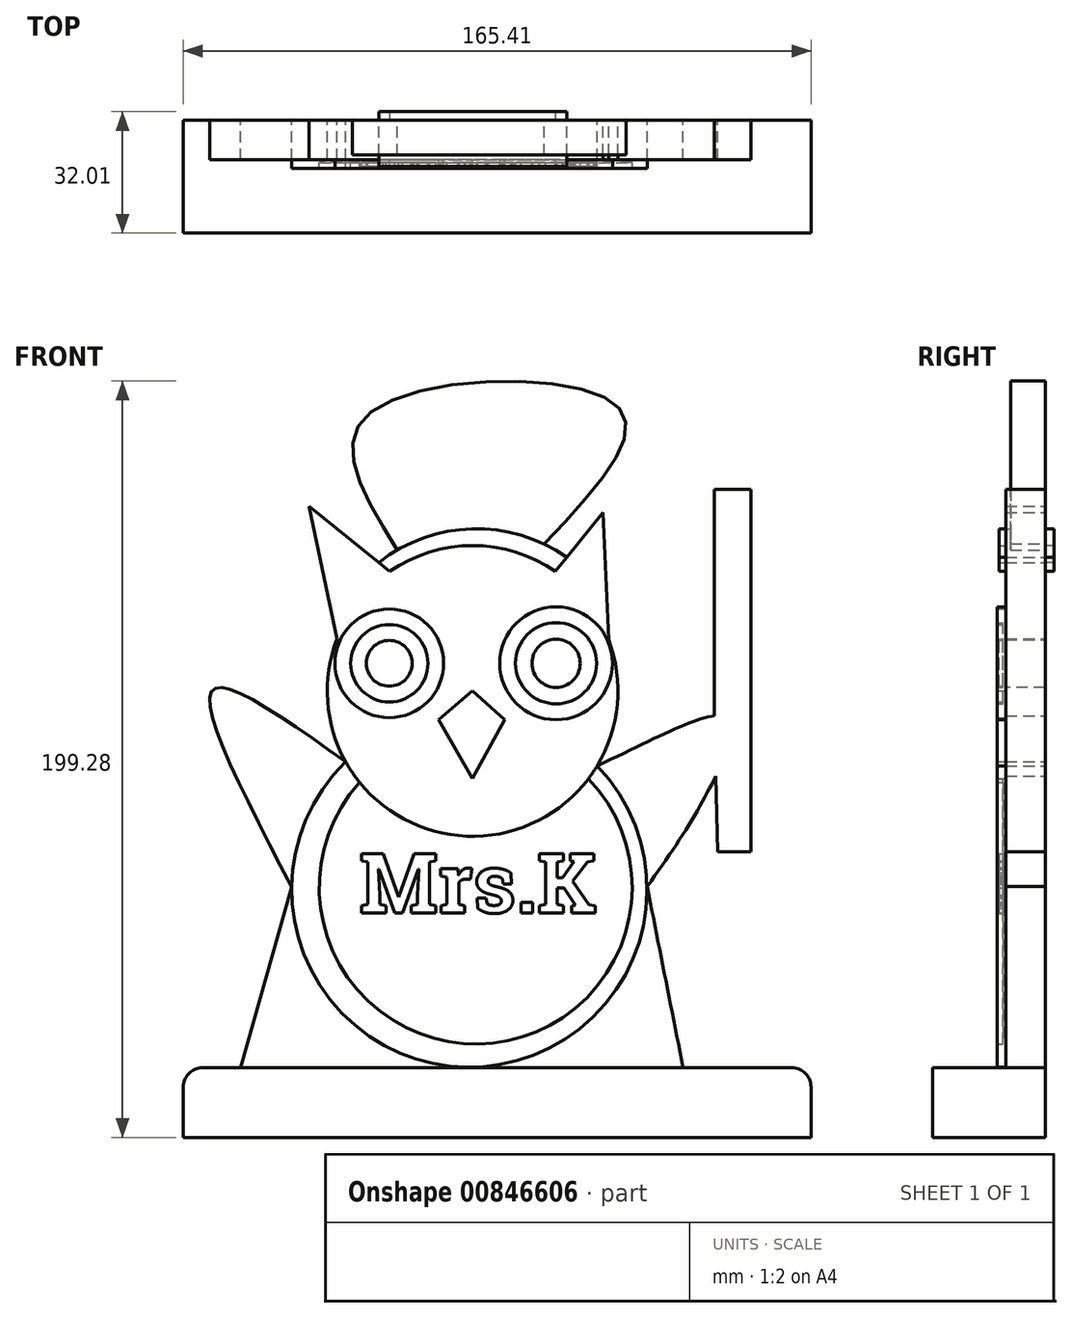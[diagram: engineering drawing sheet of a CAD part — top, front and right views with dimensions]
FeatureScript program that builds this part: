
annotation { "Feature Type Name" : "Feature", "Feature Type Description" : "" }
export const myFeature = defineFeature(function(context is Context, id is Id, definition is map)
    precondition{}
    {
        {
            var Q0;
            Q0=qCreatedBy(makeId("Front.planeOp"),FACE);
            var sketch = newSketch(context, id + "F0", { "sketchPlane" : qUnion([Q0])});
            skLineSegment(sketch, "E0.bottom", {"start": v(-76.22, -47.61) * mm, "end": v(89.19, -47.61) * mm});
            skLineSegment(sketch, "E0.top", {"start": v(-76.22, -65.94) * mm, "end": v(89.19, -65.94) * mm});
            skLineSegment(sketch, "E0.left", {"start": v(-76.22, -47.61) * mm, "end": v(-76.22, -65.94) * mm});
            skLineSegment(sketch, "E0.right", {"start": v(89.19, -47.61) * mm, "end": v(89.19, -65.94) * mm});
            skCircle(sketch, "E1", {"center": v(0, 51.72) * mm, "radius": 38.3 * mm});
            skArc(sketch, "E2", {"start": v(-33.43, 33) * mm, "mid": v(-1.58, -47.43) * mm, "end": v(32.82, 31.96) * mm});
            skArc(sketch, "E3", {"start": v(-29.76, 27.6) * mm, "mid": v(1.5, -41.3) * mm, "end": v(30.51, 28.56) * mm});
            skFitSpline(sketch, "E4", {"points": [v(-47.65, 0) * mm, v(-61.14, -47.61) * mm], "startDerivative": vector(-13.49, -47.61) * mm, "endDerivative": vector(-13.49, -47.61) * mm});
            skFitSpline(sketch, "E5", {"points": [v(45.99, 0.18) * mm, v(55.5, -47.61) * mm], "startDerivative": vector(9.56, -47.79) * mm, "endDerivative": vector(9.56, -47.79) * mm});
            skFitSpline(sketch, "E6", {"points": [v(-47.65, 0) * mm, v(-68.41, 52.03) * mm, v(-33.43, 33) * mm], "startDerivative": vector(-69.4, 133.2) * mm, "endDerivative": vector(102.73, -73.03) * mm});
            skFitSpline(sketch, "E7", {"points": [v(45.99, 0.18) * mm, v(67, 44.16) * mm, v(32.82, 31.96) * mm], "startDerivative": vector(84.02, 113.87) * mm, "endDerivative": vector(-114.08, -53.46) * mm});
            skLineSegment(sketch, "E8", {"start": v(-35.76, 65.45) * mm, "end": v(-43.12, 100.4) * mm});
            skLineSegment(sketch, "E9", {"start": v(-43.12, 100.4) * mm, "end": v(-21.83, 83.2) * mm});
            skLineSegment(sketch, "E10", {"start": v(21.83, 83.2) * mm, "end": v(34.4, 98.75) * mm});
            skLineSegment(sketch, "E11", {"start": v(34.4, 98.75) * mm, "end": v(35.85, 65.2) * mm});
            skCircle(sketch, "E12", {"center": v(-21.94, 58.99) * mm, "radius": 14.31 * mm});
            skCircle(sketch, "E13", {"center": v(-21.94, 58.99) * mm, "radius": 10.2 * mm});
            skCircle(sketch, "E14", {"center": v(-21.94, 58.99) * mm, "radius": 6.04 * mm});
            skCircle(sketch, "E15", {"center": v(22, 58.99) * mm, "radius": 14.86 * mm});
            skCircle(sketch, "E16", {"center": v(22, 58.99) * mm, "radius": 10.7 * mm});
            skCircle(sketch, "E17", {"center": v(22, 58.99) * mm, "radius": 6.35 * mm});
            skLineSegment(sketch, "E18", {"start": v(0, 51.72) * mm, "end": v(-8.98, 44.13) * mm});
            skLineSegment(sketch, "E19", {"start": v(-8.98, 44.13) * mm, "end": v(0, 28.64) * mm});
            skLineSegment(sketch, "E20", {"start": v(0, 28.64) * mm, "end": v(8.4, 44.13) * mm});
            skLineSegment(sketch, "E21", {"start": v(8.4, 44.13) * mm, "end": v(0, 51.72) * mm});
            skText(sketch, "E22", { "text": "Mrs.K", "fontName": "RobotoSlab-Bold.ttf"});
            skLineSegment(sketch, "E23", {"start": v(63.66, 44.16) * mm, "end": v(63.66, 104.79) * mm});
            skLineSegment(sketch, "E24", {"start": v(63.66, 104.79) * mm, "end": v(73.38, 104.79) * mm});
            skLineSegment(sketch, "E25", {"start": v(73.38, 104.79) * mm, "end": v(73.38, 9.38) * mm});
            skLineSegment(sketch, "E26", {"start": v(73.38, 9.38) * mm, "end": v(64.59, 9.38) * mm});
            skLineSegment(sketch, "E27", {"start": v(64.59, 9.38) * mm, "end": v(63.66, 44.16) * mm});
            skArc(sketch, "E28", {"start": v(24.85, 86.92) * mm, "mid": v(-0.18, 94.42) * mm, "end": v(-24.74, 85.55) * mm});
            skFitSpline(sketch, "E29", {"points": [v(-19.82, 88.87) * mm, v(-27.76, 124.4) * mm, v(38.2, 126.66) * mm, v(18.85, 90.41) * mm], "startDerivative": vector(-86.87, 139.97) * mm, "endDerivative": vector(-130.42, -137.65) * mm});
            const initialGuessF0  = {"E22": [-0.02985, -0.00677, 1, 0, 0.0158]};
            skSetInitialGuess(sketch, initialGuessF0);
            skSolve(sketch);
        }
        {
            var Q0;
            Q0=makeQuery(id+"F0.imprint","IMPRINT",FACE,{"disambiguationData":[TD([[makeQuery(id+"F0.imprint","IMPRINT",EDGE,{"derivedFrom":sQuery(id+"F0.wireOp",EDGE,"E0.top")}),1.0]])]});
            extrude(context, id + "F1", {"entities" : qUnion([Q0]), "depth" : 29.72 * mm, "offsetDistance" : 25.4 * mm});
        }
        {
            var Q0;
            {var subQ0=sQuery(id+"F0.wireOp",EDGE,"E6");Q0=makeQuery(id+"F0.imprint","IMPRINT",FACE,{"disambiguationData":[TD([[makeQuery(id+"F0.imprint","IMPRINT",EDGE,{"derivedFrom":subQ0}),-1.0]])]});}
            var Q1;
            {var subQ0=sQuery(id+"F0.wireOp",EDGE,"E8");Q1=makeQuery(id+"F0.imprint","IMPRINT",FACE,{"disambiguationData":[TD([[makeQuery(id+"F0.imprint","IMPRINT",EDGE,{"derivedFrom":subQ0}),-1.0]])]});}
            var Q2;
            {var subQ0=sQuery(id+"F0.wireOp",EDGE,"E10");Q2=makeQuery(id+"F0.imprint","IMPRINT",FACE,{"disambiguationData":[TD([[makeQuery(id+"F0.imprint","IMPRINT",EDGE,{"derivedFrom":subQ0}),-1.0]])]});}
            var Q3;
            Q3=makeQuery(id+"F0.imprint","IMPRINT",FACE,{"disambiguationData":[TD([[makeQuery(id+"F0.imprint","IMPRINT",EDGE,{"derivedFrom":sQuery(id+"F0.wireOp",EDGE,"E12")}),-1.0]])]});
            var Q4;
            {var subQ0=sQuery(id+"F0.wireOp",EDGE,"E7");Q4=makeQuery(id+"F0.imprint","IMPRINT",FACE,{"disambiguationData":[TD([[makeQuery(id+"F0.imprint","IMPRINT",EDGE,{"derivedFrom":subQ0}),1.0]])]});}
            var Q5;
            {var subQ0=sQuery(id+"F0.wireOp",EDGE,"E4");Q5=makeQuery(id+"F0.imprint","IMPRINT",FACE,{"disambiguationData":[TD([[makeQuery(id+"F0.imprint","IMPRINT",EDGE,{"derivedFrom":subQ0}),1.0]])]});}
            extrude(context, id + "F2", {"entities" : qUnion([Q0, Q1, Q2, Q3, Q4, Q5]), "operationType" : NewBodyOperationType.ADD, "depth" : 10.4 * mm, "offsetDistance" : 25.4 * mm});
        }
        {
            var Q0;
            Q0=makeQuery(id+"F0.imprint","IMPRINT",FACE,{"disambiguationData":[TD([[makeQuery(id+"F0.imprint","IMPRINT",EDGE,{"derivedFrom":sQuery(id+"F0.wireOp",EDGE,"E12")}),1.0]])]});
            var Q1;
            Q1=makeQuery(id+"F0.imprint","IMPRINT",FACE,{"disambiguationData":[TD([[makeQuery(id+"F0.imprint","IMPRINT",EDGE,{"derivedFrom":sQuery(id+"F0.wireOp",EDGE,"E15")}),1.0]])]});
            var Q2;
            Q2=makeQuery(id+"F0.imprint","IMPRINT",FACE,{"disambiguationData":[TD([[makeQuery(id+"F0.imprint","IMPRINT",EDGE,{"derivedFrom":sQuery(id+"F0.wireOp",EDGE,"E18")}),1.0]])]});
            var Q3;
            {var subQ7=sQuery(id+"F0.wireOp",EDGE,"E3");Q3=makeQuery(id+"F0.imprint","IMPRINT",FACE,{"disambiguationData":[TD([[makeQuery(id+"F0.imprint","IMPRINT",EDGE,{"derivedFrom":subQ7}),-1.0]])]});}
            extrude(context, id + "F3", {"entities" : qUnion([Q0, Q1, Q2, Q3]), "operationType" : NewBodyOperationType.ADD, "depth" : 12.7 * mm, "offsetDistance" : 25.4 * mm});
        }
        {
            var Q0;
            Q0=makeQuery(id+"F0.imprint","IMPRINT",FACE,{"disambiguationData":[TD([[makeQuery(id+"F0.imprint","IMPRINT",EDGE,{"derivedFrom":sQuery(id+"F0.wireOp",EDGE,"E16")}),1.0]])]});
            var Q1;
            Q1=makeQuery(id+"F0.imprint","IMPRINT",FACE,{"disambiguationData":[TD([[makeQuery(id+"F0.imprint","IMPRINT",EDGE,{"derivedFrom":sQuery(id+"F0.wireOp",EDGE,"E13")}),1.0]])]});
            var Q2;
            {var subQ0=sQuery(id+"F0.wireOp",EDGE,"E3");Q2=makeQuery(id+"F0.imprint","IMPRINT",FACE,{"disambiguationData":[TD([[makeQuery(id+"F0.imprint","IMPRINT",EDGE,{"derivedFrom":subQ0}),1.0]])]});}
            extrude(context, id + "F4", {"entities" : qUnion([Q0, Q1, Q2]), "operationType" : NewBodyOperationType.ADD, "depth" : 11.18 * mm, "offsetDistance" : 25.4 * mm});
        }
        {
            var Q0;
            Q0=makeQuery(id+"F0.imprint","IMPRINT",FACE,{"disambiguationData":[TD([[makeQuery(id+"F0.imprint","IMPRINT",EDGE,{"derivedFrom":sQuery(id+"F0.wireOp",EDGE,"E14")}),1.0]])]});
            var Q1;
            Q1=makeQuery(id+"F0.imprint","IMPRINT",FACE,{"disambiguationData":[TD([[makeQuery(id+"F0.imprint","IMPRINT",EDGE,{"derivedFrom":sQuery(id+"F0.wireOp",EDGE,"E17")}),1.0]])]});
            var Q2;
            Q2=makeQuery(id+"F0.imprint","IMPRINT",FACE,{"disambiguationData":[TD([[makeQuery(id+"F0.imprint","IMPRINT",EDGE,{"derivedFrom":sQuery(id+"F0.wireOp",EDGE,"E22.sketch_text.stroke-0")}),-1.0]])]});
            var Q3;
            Q3=makeQuery(id+"F0.imprint","IMPRINT",FACE,{"disambiguationData":[TD([[makeQuery(id+"F0.imprint","IMPRINT",EDGE,{"derivedFrom":sQuery(id+"F0.wireOp",EDGE,"E22.sketch_text.stroke-31")}),-1.0]])]});
            var Q4;
            Q4=makeQuery(id+"F0.imprint","IMPRINT",FACE,{"disambiguationData":[TD([[makeQuery(id+"F0.imprint","IMPRINT",EDGE,{"derivedFrom":sQuery(id+"F0.wireOp",EDGE,"E22.sketch_text.stroke-50")}),-1.0]])]});
            var Q5;
            Q5=makeQuery(id+"F0.imprint","IMPRINT",FACE,{"disambiguationData":[TD([[makeQuery(id+"F0.imprint","IMPRINT",EDGE,{"derivedFrom":sQuery(id+"F0.wireOp",EDGE,"E22.sketch_text.stroke-80")}),-1.0]])]});
            var Q6;
            Q6=makeQuery(id+"F0.imprint","IMPRINT",FACE,{"disambiguationData":[TD([[makeQuery(id+"F0.imprint","IMPRINT",EDGE,{"derivedFrom":sQuery(id+"F0.wireOp",EDGE,"E22.sketch_text.stroke-84")}),-1.0]])]});
            extrude(context, id + "F5", {"entities" : qUnion([Q0, Q1, Q2, Q3, Q4, Q5, Q6]), "operationType" : NewBodyOperationType.ADD, "depth" : 12.2 * mm, "offsetDistance" : 25.4 * mm});
        }
        {
            var Q0;
            Q0=makeQuery(id+"F1.opExtrude","SWEPT_EDGE",EDGE,{"disambiguationData":[OSD([sQuery(id+"F0.wireOp",EDGE,"E0.bottom"),sQuery(id+"F0.wireOp",EDGE,"E0.right")])]});
            var Q1;
            Q1=makeQuery(id+"F1.opExtrude","SWEPT_EDGE",EDGE,{"disambiguationData":[OSD([sQuery(id+"F0.wireOp",EDGE,"E0.bottom"),sQuery(id+"F0.wireOp",EDGE,"E0.left")])]});
            fillet(context, id + "F6", {"entities" : qUnion([Q0, Q1]), "radius" : 5.08 * mm, "tangentPropagation" : true, "allowEdgeOverflow" : false});
        }
        {
            var Q0;
            {var subQ5=sQuery(id+"F0.wireOp",EDGE,"E1");var subQ7=sQuery(id+"F0.wireOp",EDGE,"E9");var subQ8=makeQuery(id+"F0.imprint","INTERSECT",VERTEX,{"derivedFrom":[subQ5,subQ7]});Q0=makeQuery(id+"F0.imprint","IMPRINT",FACE,{"disambiguationData":[TD([[makeQuery(id+"F0.imprint","IMPRINT",EDGE,{"disambiguationData":[TD([[subQ8,1.0]])],"derivedFrom":subQ5}),-1.0]])]});}
            extrude(context, id + "F7", {"entities" : qUnion([Q0]), "operationType" : NewBodyOperationType.ADD, "depth" : 12.2 * mm, "offsetDistance" : 25.4 * mm});
        }
        {
            var Q0;
            {var subQ5=sQuery(id+"F0.wireOp",EDGE,"E1");var subQ7=sQuery(id+"F0.wireOp",EDGE,"E9");var subQ8=makeQuery(id+"F0.imprint","INTERSECT",VERTEX,{"derivedFrom":[subQ5,subQ7]});Q0=makeQuery(id+"F0.imprint","IMPRINT",FACE,{"disambiguationData":[TD([[makeQuery(id+"F0.imprint","IMPRINT",EDGE,{"disambiguationData":[TD([[subQ8,1.0]])],"derivedFrom":subQ5}),-1.0]])]});}
            extrude(context, id + "F8", {"entities" : qUnion([Q0]), "operationType" : NewBodyOperationType.ADD, "oppositeDirection" : true, "depth" : 2.3 * mm, "offsetDistance" : 25.4 * mm});
        }
        {
            var Q0;
            {var subQ0=sQuery(id+"F0.wireOp",EDGE,"E29");Q0=makeQuery(id+"F0.imprint","IMPRINT",FACE,{"disambiguationData":[TD([[makeQuery(id+"F0.imprint","IMPRINT",EDGE,{"derivedFrom":subQ0}),-1.0]])]});}
            extrude(context, id + "F9", {"entities" : qUnion([Q0]), "operationType" : NewBodyOperationType.ADD, "depth" : 9.14 * mm, "offsetDistance" : 25.4 * mm});
        }
        {
            var Q0;
            {var subQ1=sQuery(id+"F0.wireOp",EDGE,"E23");Q0=makeQuery(id+"F0.imprint","IMPRINT",FACE,{"disambiguationData":[TD([[makeQuery(id+"F0.imprint","IMPRINT",EDGE,{"derivedFrom":subQ1}),-1.0]])]});}
            extrude(context, id + "F10", {"entities" : qUnion([Q0]), "depth" : 6.35 * mm, "offsetDistance" : 25.4 * mm});
        }
        {
            var Q0;
            Q0=makeQuery(id+"F10.opExtrude","CAP_FACE",FACE,{"disambiguationData":[OSD([sQuery(id+"F0.wireOp",EDGE,"E7"),sQuery(id+"F0.wireOp",EDGE,"E23"),sQuery(id+"F0.wireOp",EDGE,"E24"),sQuery(id+"F0.wireOp",EDGE,"E25"),sQuery(id+"F0.wireOp",EDGE,"E26"),sQuery(id+"F0.wireOp",EDGE,"E27")])],"isStart":false});
            extrude(context, id + "F11", {"entities" : qUnion([Q0]), "operationType" : NewBodyOperationType.ADD, "oppositeDirection" : true, "depth" : 1.78 * mm, "offsetDistance" : 25.4 * mm});
        }
        {
            var Q0;
            Q0=makeQuery(id+"F10.opExtrude","CAP_FACE",FACE,{"disambiguationData":[OSD([sQuery(id+"F0.wireOp",EDGE,"E7"),sQuery(id+"F0.wireOp",EDGE,"E23"),sQuery(id+"F0.wireOp",EDGE,"E27")])],"isStart":false});
            extrude(context, id + "F12", {"entities" : qUnion([Q0]), "operationType" : NewBodyOperationType.ADD, "depth" : 4.06 * mm, "offsetDistance" : 25.4 * mm});
        }
        {
            var Q0;
            {var subQ0=sQuery(id+"F0.wireOp",EDGE,"E24");Q0=makeQuery(id+"F0.imprint","IMPRINT",FACE,{"disambiguationData":[TD([[makeQuery(id+"F0.imprint","IMPRINT",EDGE,{"derivedFrom":subQ0}),-1.0]])]});}
            extrude(context, id + "F13", {"entities" : qUnion([Q0]), "operationType" : NewBodyOperationType.ADD, "depth" : 10.4 * mm, "offsetDistance" : 25.4 * mm});
        }
    });
